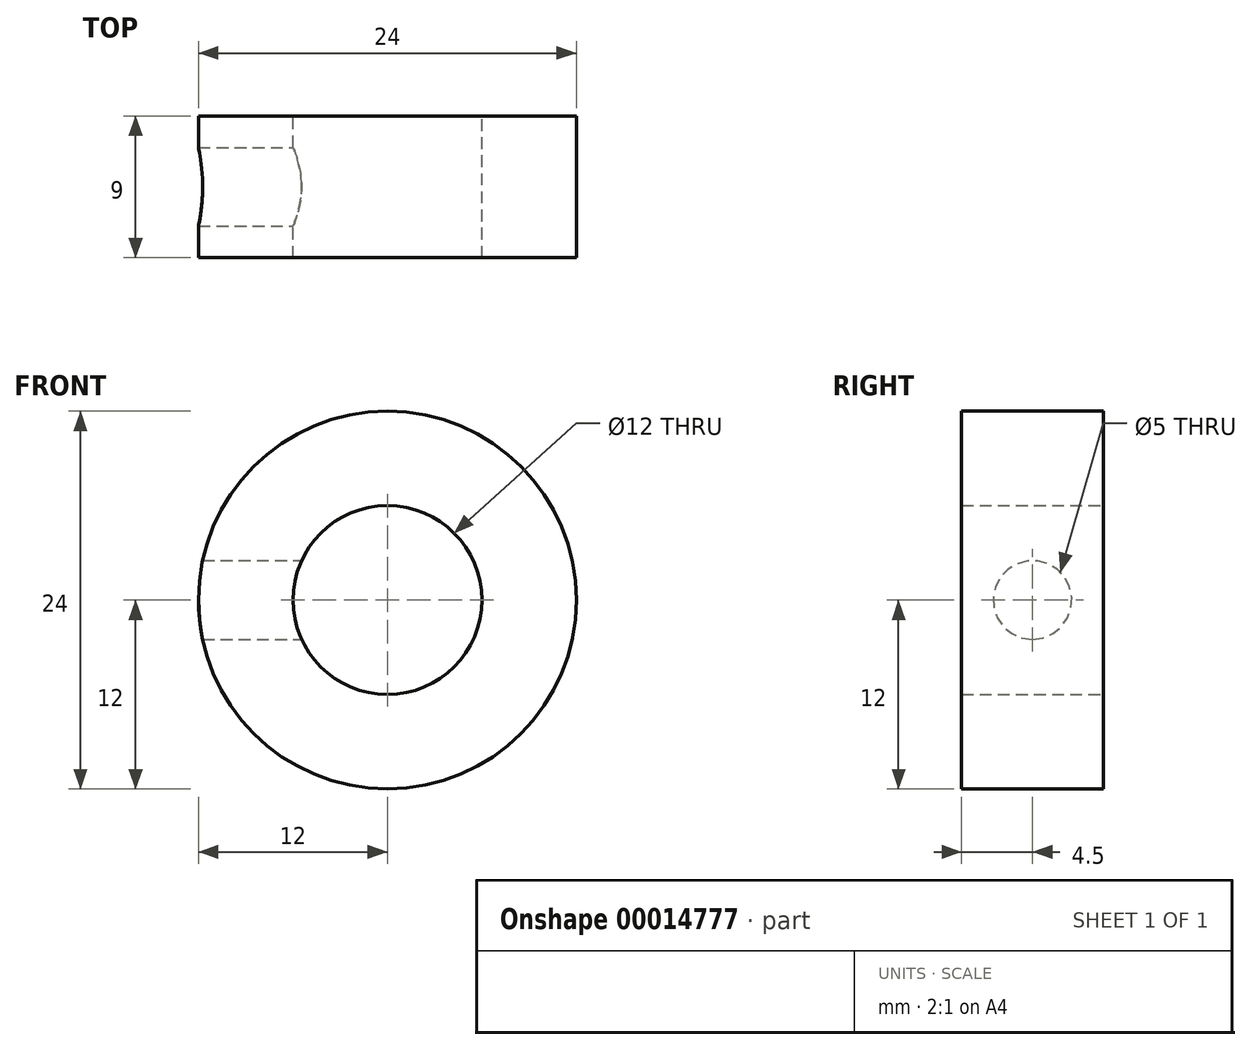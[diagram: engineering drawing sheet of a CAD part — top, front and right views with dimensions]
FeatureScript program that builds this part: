
annotation { "Feature Type Name" : "Feature", "Feature Type Description" : "" }
export const myFeature = defineFeature(function(context is Context, id is Id, definition is map)
    precondition{}
    {
        {
            var Q0;
            Q0=qCreatedBy(makeId("Front.planeOp"),FACE);
            var sketch = newSketch(context, id + "F0", { "sketchPlane" : qUnion([Q0])});
            skCircle(sketch, "E0", {"center": v(0, 0) * mm, "radius": 6 * mm});
            skCircle(sketch, "E1.0", {"center": v(0, 0) * mm, "radius": 12 * mm});
            skSolve(sketch);
        }
        {
            var Q0;
            Q0=makeQuery(id+"F0.imprint","IMPRINT",FACE,{"disambiguationData":[TD([[makeQuery(id+"F0.imprint","IMPRINT",EDGE,{"derivedFrom":sQuery(id+"F0.wireOp",EDGE,"E0")}),-1.0]])]});
            extrude(context, id + "F1", {"entities" : qUnion([Q0]), "endBound" : BoundingType.SYMMETRIC, "depth" : 9 * mm});
        }
        {
            var Q0;
            Q0=qCreatedBy(makeId("Right.planeOp"),FACE);
            var sketch = newSketch(context, id + "F2", { "sketchPlane" : qUnion([Q0])});
            skCircle(sketch, "E2", {"center": v(0, 0) * mm, "radius": 2.5 * mm});
            skSolve(sketch);
        }
        {
            var Q0;
            Q0 = qSketchRegion(id + "F2", true);
            var Q1;
            Q1=makeQuery(id+"F1.opExtrude","SWEPT_FACE",FACE,{"disambiguationData":[OSD([sQuery(id+"F0.wireOp",EDGE,"E1.0")])]});
            extrude(context, id + "F3", {"entities" : qUnion([Q0]), "operationType" : NewBodyOperationType.REMOVE, "endBound" : BoundingType.UP_TO_SURFACE, "oppositeDirection" : true, "endBoundEntityFace" : qUnion([Q1]), "depth" : 25 * mm});
        }
    });
